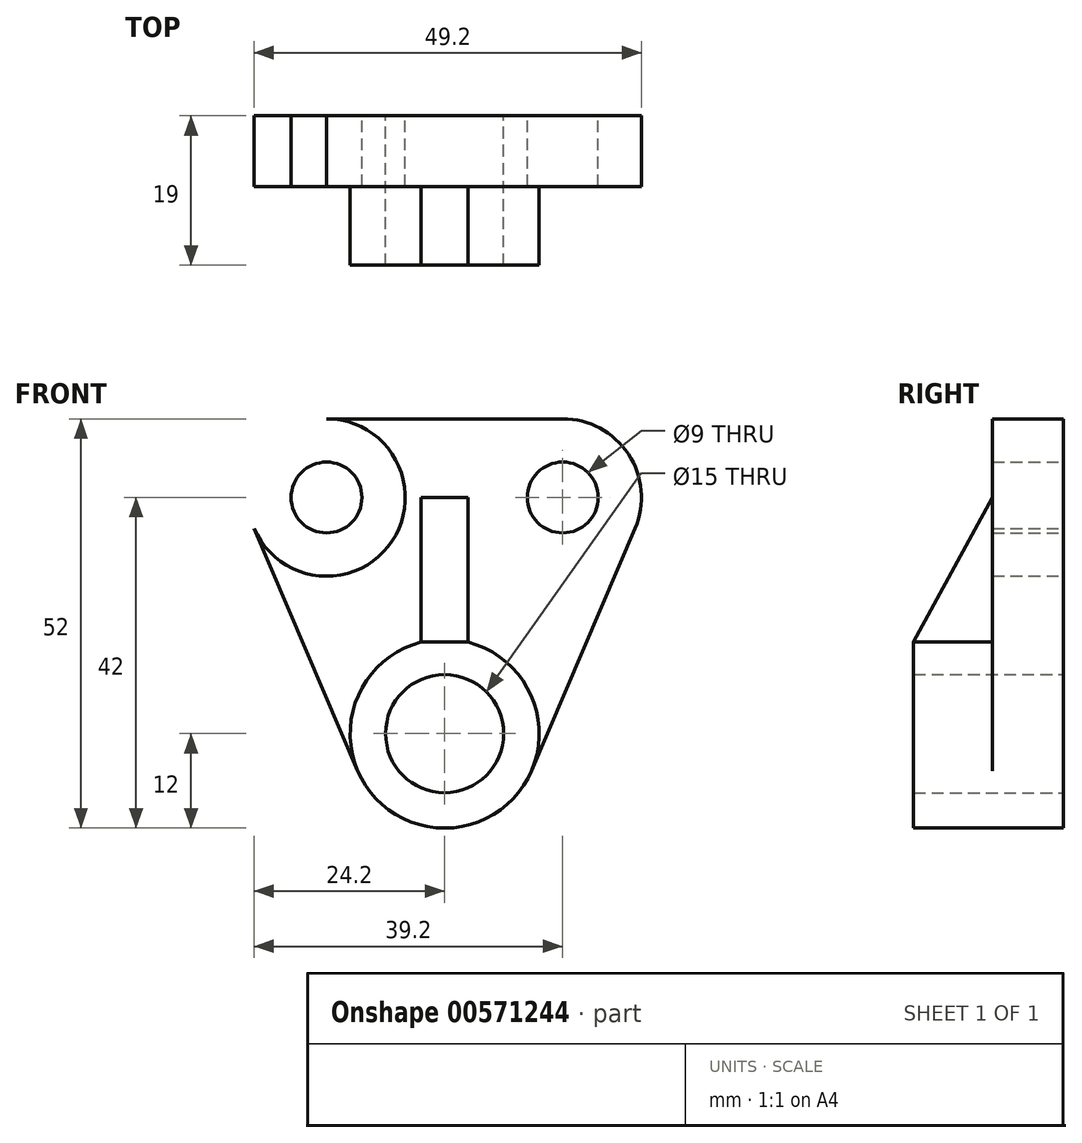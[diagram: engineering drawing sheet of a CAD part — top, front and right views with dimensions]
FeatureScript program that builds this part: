
annotation { "Feature Type Name" : "Feature", "Feature Type Description" : "" }
export const myFeature = defineFeature(function(context is Context, id is Id, definition is map)
    precondition{}
    {
        {
            var Q0;
            Q0=qCreatedBy(makeId("Front.planeOp"),FACE);
            var sketch = newSketch(context, id + "F0", { "sketchPlane" : qUnion([Q0])});
            skCircle(sketch, "E0", {"center": v(0, 0) * mm, "radius": 7.5 * mm});
            skCircle(sketch, "E1", {"center": v(0, 0) * mm, "radius": 12 * mm});
            skCircle(sketch, "E2", {"center": v(15, 30) * mm, "radius": 4.5 * mm});
            skCircle(sketch, "E3.MirrorC", {"center": v(-15, 30) * mm, "radius": 4.5 * mm});
            skCircle(sketch, "E4", {"center": v(15, 30) * mm, "radius": 10 * mm});
            skCircle(sketch, "E5", {"center": v(-15, 30) * mm, "radius": 10 * mm});
            skLineSegment(sketch, "E6", {"start": v(24.2, 26.07) * mm, "end": v(11.03, -4.72) * mm});
            skLineSegment(sketch, "E7", {"start": v(-24.2, 26.07) * mm, "end": v(-11.03, -4.72) * mm});
            skLineSegment(sketch, "E8", {"start": v(-15, 40) * mm, "end": v(15, 40) * mm});
            skLineSegment(sketch, "E9", {"start": v(-3, 11.62) * mm, "end": v(-3, 30) * mm});
            skLineSegment(sketch, "E10", {"start": v(-3, 30) * mm, "end": v(3, 30) * mm});
            skLineSegment(sketch, "E11", {"start": v(3, 30) * mm, "end": v(3, 11.62) * mm});
            skSolve(sketch);
        }
        {
            var Q0;
            {var subQ0=sQuery(id+"F0.wireOp",EDGE,"E9");Q0=makeQuery(id+"F0.imprint","IMPRINT",FACE,{"disambiguationData":[TD([[makeQuery(id+"F0.imprint","IMPRINT",EDGE,{"derivedFrom":subQ0}),-1.0]])]});}
            var Q1;
            {var subQ3=sQuery(id+"F0.wireOp",EDGE,"E6");Q1=makeQuery(id+"F0.imprint","IMPRINT",FACE,{"disambiguationData":[TD([[makeQuery(id+"F0.imprint","IMPRINT",EDGE,{"derivedFrom":subQ3}),-1.0]])]});}
            var Q2;
            Q2=makeQuery(id+"F0.imprint","IMPRINT",FACE,{"disambiguationData":[TD([[makeQuery(id+"F0.imprint","IMPRINT",EDGE,{"derivedFrom":sQuery(id+"F0.wireOp",EDGE,"E3.MirrorC")}),1.0]])]});
            var Q3;
            Q3=makeQuery(id+"F0.imprint","IMPRINT",FACE,{"disambiguationData":[TD([[makeQuery(id+"F0.imprint","IMPRINT",EDGE,{"derivedFrom":sQuery(id+"F0.wireOp",EDGE,"E2")}),-1.0]])]});
            extrude(context, id + "F1", {"entities" : qUnion([Q0, Q1, Q2, Q3]), "depth" : 9 * mm, "offsetDistance" : 25 * mm});
        }
        {
            var Q0;
            {var subQ0=sQuery(id+"F0.wireOp",EDGE,"E9");Q0=makeQuery(id+"F0.imprint","IMPRINT",FACE,{"disambiguationData":[TD([[makeQuery(id+"F0.imprint","IMPRINT",EDGE,{"derivedFrom":subQ0}),-1.0]])]});}
            extrude(context, id + "F2", {"entities" : qUnion([Q0]), "operationType" : NewBodyOperationType.ADD, "depth" : 19 * mm, "offsetDistance" : 25 * mm});
        }
        {
            var Q0;
            Q0=makeQuery(id+"F2.opExtrude","SWEPT_FACE",FACE,{"disambiguationData":[OSD([sQuery(id+"F0.wireOp",EDGE,"E9")])]});
            var sketch = newSketch(context, id + "F3", { "sketchPlane" : qUnion([Q0])});
            skLineSegment(sketch, "E12", {"start": v(9, 30) * mm, "end": v(19, 11.62) * mm});
            skSolve(sketch);
        }
        {
            var Q0;
            Q0=makeQuery(id+"F0.imprint","IMPRINT",FACE,{"disambiguationData":[TD([[makeQuery(id+"F0.imprint","IMPRINT",EDGE,{"derivedFrom":sQuery(id+"F0.wireOp",EDGE,"E0")}),-1.0]])]});
            extrude(context, id + "F4", {"entities" : qUnion([Q0]), "operationType" : NewBodyOperationType.ADD, "depth" : 19 * mm, "offsetDistance" : 25 * mm});
        }
        {
            var Q0;
            Q0=makeQuery(id+"F3.imprint","IMPRINT",FACE,{"disambiguationData":[TD([[makeQuery(id+"F3.imprint","IMPRINT",EDGE,{"derivedFrom":sQuery(id+"F3.wireOp",EDGE,"E12")}),1.0]])]});
            extrude(context, id + "F5", {"entities" : qUnion([Q0]), "operationType" : NewBodyOperationType.REMOVE, "endBound" : BoundingType.THROUGH_ALL, "oppositeDirection" : true, "depth" : 25 * mm, "offsetDistance" : 25 * mm});
        }
    });
